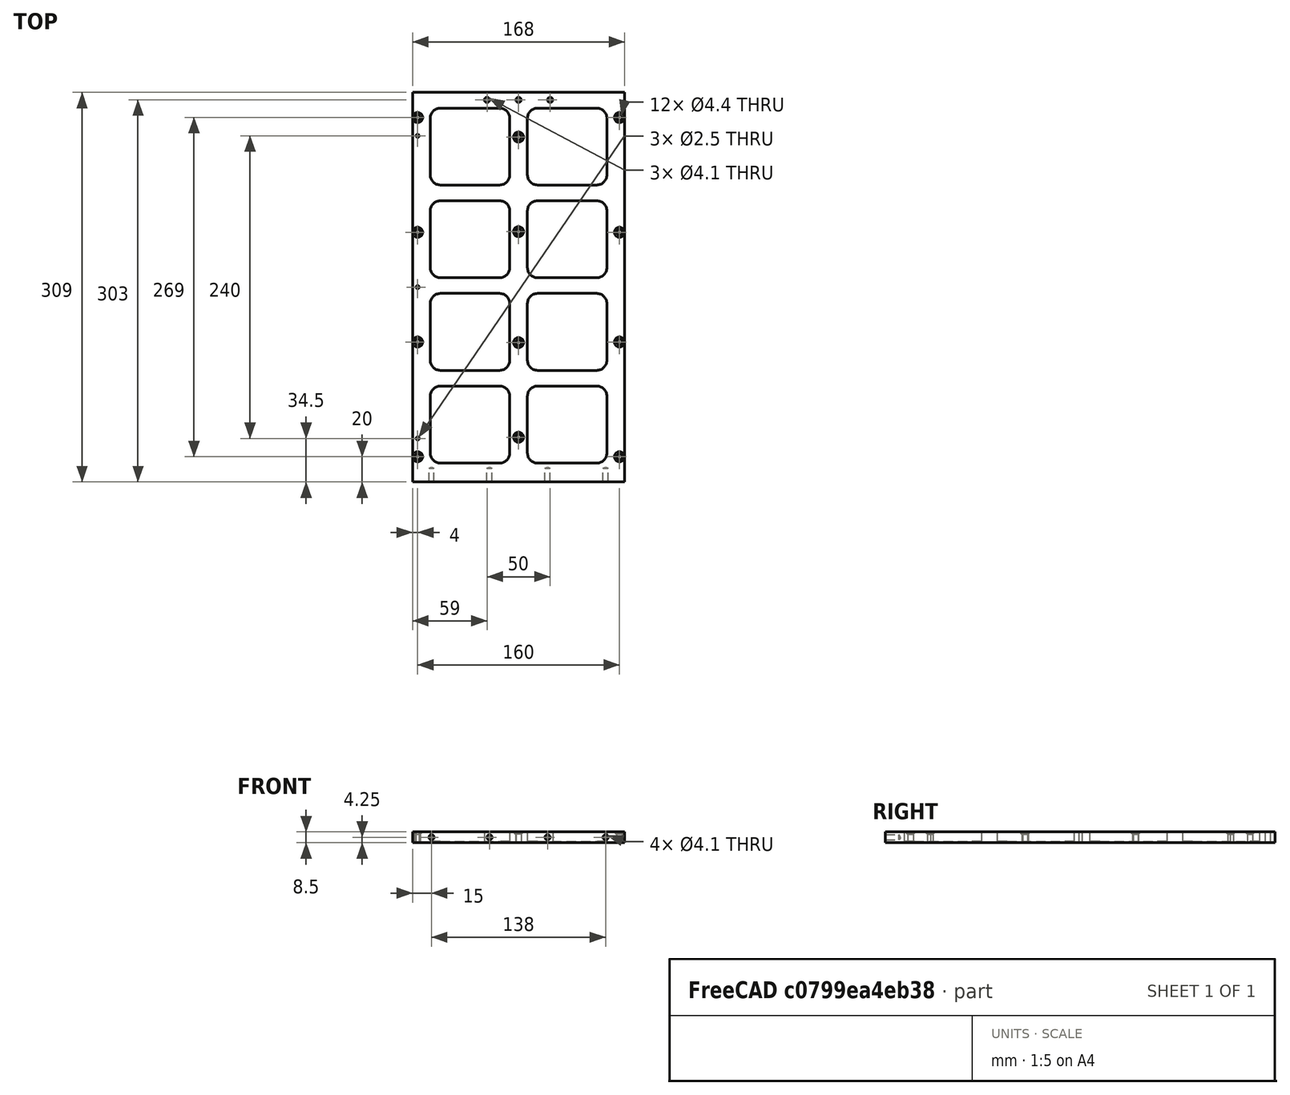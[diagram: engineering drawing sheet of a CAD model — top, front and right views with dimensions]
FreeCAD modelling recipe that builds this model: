
FCSTD DOCUMENT  (FreeCAD 0.18R14555 (Git shallow))
Label: y-plate
License: All rights reserved
LicenseURL: http://en.wikipedia.org/wiki/All_rights_reserved
objects: Sketcher::SketchObject×7, PartDesign::Hole×5, TechDraw::DrawViewDimension×4, TechDraw::DrawViewAnnotation×2, PartDesign::Pad×1, PartDesign::Pocket×1, PartDesign::Mirrored×1, PartDesign::Plane×1, PartDesign::Body×1, TechDraw::DrawSVGTemplate×1, TechDraw::DrawViewPart×1, TechDraw::DrawProjGroupItem×1, TechDraw::DrawProjGroup×1, TechDraw::DrawViewSection×1, TechDraw::DrawPage×1
note: 24 computed .brp shape members not serialized (recipe doc carries the construction recipe); baked Part::Feature solids carry a one-line shape summary decoded from their .brp

FEATURE [Sketcher::SketchObject] Sketch  label="plate"
  MapMode = 5
  Support = -> [XY_Plane]
  sketch-geometry (4):
    g0: LineSegment StartX=-84 StartY=154.5 StartZ=0 EndX=84 EndY=154.5 EndZ=0
    g1: LineSegment StartX=84 StartY=154.5 StartZ=0 EndX=84 EndY=-154.5 EndZ=0
    g2: LineSegment StartX=84 StartY=-154.5 StartZ=0 EndX=-84 EndY=-154.5 EndZ=0
    g3: LineSegment StartX=-84 StartY=-154.5 StartZ=0 EndX=-84 EndY=154.5 EndZ=0
  constraints (10):
    c: Coincident(g0,g1)
    c: Coincident(g1,g2)
    c: Coincident(g2,g3)
    c: Coincident(g3,g0)
    c: Horizontal(g2)
    c: Vertical(g3)
    c: DistanceY(g1,g1) = 309  'length'
    c: Symmetric(g0,g0,g-2)
    c: Symmetric(g1,g0,g-1)
    c: DistanceX(g0,g0) = 168  'width'
FEATURE [PartDesign::Pad] Pad
  Length = 8.5
  Length2 = 100
  Profile = -> Sketch
  Reversed = true
  Type = 0
FEATURE [Sketcher::SketchObject] Sketch001
  MapMode = 5
  Support = -> [XY_Plane]
  sketch-geometry (79):
    g0: LineSegment StartX=-62 StartY=-78.5 StartZ=0 EndX=-15 EndY=-78.5 EndZ=0
    g1: LineSegment StartX=-7 StartY=-86.5 StartZ=0 EndX=-7 EndY=-131.5 EndZ=0
    g2: LineSegment StartX=-15 StartY=-139.5 StartZ=0 EndX=-62 EndY=-139.5 EndZ=0
    g3: LineSegment StartX=-70 StartY=-131.5 StartZ=0 EndX=-70 EndY=-86.5 EndZ=0
    g4: ArcOfCircle CenterX=-15 CenterY=-86.5 CenterZ=0 NormalX=0 NormalY=0 NormalZ=1 AngleXU=0 Radius=8 StartAngle=1.7e-15 EndAngle=1.5708
    g5: ArcOfCircle CenterX=-15 CenterY=-131.5 CenterZ=0 NormalX=0 NormalY=0 NormalZ=1 AngleXU=0 Radius=8 StartAngle=4.71239 EndAngle=6.28319
    g6: ArcOfCircle CenterX=-62 CenterY=-131.5 CenterZ=0 NormalX=0 NormalY=0 NormalZ=1 AngleXU=0 Radius=8 StartAngle=3.14159 EndAngle=4.71239
    g7: ArcOfCircle CenterX=-62 CenterY=-86.5 CenterZ=0 NormalX=0 NormalY=0 NormalZ=1 AngleXU=0 Radius=8 StartAngle=1.5708 EndAngle=3.14159
    g8: LineSegment StartX=15 StartY=-78.5 StartZ=0 EndX=62 EndY=-78.5 EndZ=0
    g9: LineSegment StartX=70 StartY=-86.5 StartZ=0 EndX=70 EndY=-131.5 EndZ=0
    g10: LineSegment StartX=62 StartY=-139.5 StartZ=0 EndX=15 EndY=-139.5 EndZ=0
    g11: LineSegment StartX=7 StartY=-131.5 StartZ=0 EndX=7 EndY=-86.5 EndZ=0
    g12: ArcOfCircle CenterX=62 CenterY=-86.5 CenterZ=0 NormalX=0 NormalY=0 NormalZ=1 AngleXU=0 Radius=8 StartAngle=-1.8e-15 EndAngle=1.5708
    g13: ArcOfCircle CenterX=62 CenterY=-131.5 CenterZ=0 NormalX=0 NormalY=0 NormalZ=1 AngleXU=0 Radius=8 StartAngle=4.71239 EndAngle=6.28319
    g14: ArcOfCircle CenterX=15 CenterY=-131.5 CenterZ=0 NormalX=0 NormalY=0 NormalZ=1 AngleXU=0 Radius=8 StartAngle=3.14159 EndAngle=4.71239
    g15: ArcOfCircle CenterX=15 CenterY=-86.5 CenterZ=0 NormalX=0 NormalY=0 NormalZ=1 AngleXU=0 Radius=8 StartAngle=1.5708 EndAngle=3.14159
    g16: LineSegment [constr] StartX=7 StartY=-86.5 StartZ=0 EndX=-7 EndY=-86.5 EndZ=0
    g17: LineSegment [constr] StartX=84 StartY=-131.5 StartZ=0 EndX=-84 EndY=-131.5 EndZ=0
    g18: LineSegment [constr] StartX=84 StartY=-131.5 StartZ=0 EndX=70 EndY=-131.5 EndZ=0
    g19: LineSegment [constr] StartX=-84 StartY=-131.5 StartZ=0 EndX=-70 EndY=-131.5 EndZ=0
    g20: LineSegment StartX=-62 StartY=-5 StartZ=0 EndX=-15 EndY=-5 EndZ=0
    g21: LineSegment StartX=-7 StartY=-13 StartZ=0 EndX=-7 EndY=-58 EndZ=0
    g22: LineSegment StartX=-15 StartY=-66 StartZ=0 EndX=-62 EndY=-66 EndZ=0
    g23: LineSegment StartX=-70 StartY=-58 StartZ=0 EndX=-70 EndY=-13 EndZ=0
    g24: ArcOfCircle CenterX=-15 CenterY=-13 CenterZ=0 NormalX=0 NormalY=0 NormalZ=1 AngleXU=0 Radius=8 StartAngle=-1.8e-15 EndAngle=1.5708
    g25: ArcOfCircle CenterX=-15 CenterY=-58 CenterZ=0 NormalX=0 NormalY=0 NormalZ=1 AngleXU=0 Radius=8 StartAngle=4.71239 EndAngle=6.28319
    g26: ArcOfCircle CenterX=-62 CenterY=-58 CenterZ=0 NormalX=0 NormalY=0 NormalZ=1 AngleXU=0 Radius=8 StartAngle=3.14159 EndAngle=4.71239
    g27: ArcOfCircle CenterX=-62 CenterY=-13 CenterZ=0 NormalX=0 NormalY=0 NormalZ=1 AngleXU=0 Radius=8 StartAngle=1.5708 EndAngle=3.14159
    g28: LineSegment StartX=15 StartY=-5 StartZ=0 EndX=62 EndY=-5 EndZ=0
    g29: LineSegment StartX=70 StartY=-13 StartZ=0 EndX=70 EndY=-58 EndZ=0
    g30: LineSegment StartX=62 StartY=-66 StartZ=0 EndX=15 EndY=-66 EndZ=0
    g31: LineSegment StartX=7 StartY=-58 StartZ=0 EndX=7 EndY=-13 EndZ=0
    g32: ArcOfCircle CenterX=62 CenterY=-13 CenterZ=0 NormalX=0 NormalY=0 NormalZ=1 AngleXU=0 Radius=8 StartAngle=-9e-16 EndAngle=1.5708
    g33: ArcOfCircle CenterX=62 CenterY=-58 CenterZ=0 NormalX=0 NormalY=0 NormalZ=1 AngleXU=0 Radius=8 StartAngle=4.71239 EndAngle=6.28319
    g34: ArcOfCircle CenterX=15 CenterY=-58 CenterZ=0 NormalX=0 NormalY=0 NormalZ=1 AngleXU=0 Radius=8 StartAngle=3.14159 EndAngle=4.71239
    g35: ArcOfCircle CenterX=15 CenterY=-13 CenterZ=0 NormalX=0 NormalY=0 NormalZ=1 AngleXU=0 Radius=8 StartAngle=1.5708 EndAngle=3.14159
    g36: LineSegment [constr] StartX=-62 StartY=-154.5 StartZ=0 EndX=-62 EndY=154.5 EndZ=0
    g37: LineSegment StartX=-62 StartY=68.5 StartZ=0 EndX=-15 EndY=68.5 EndZ=0
    g38: LineSegment StartX=-7 StartY=60.5 StartZ=0 EndX=-7 EndY=15.5 EndZ=0
    g39: LineSegment StartX=-15 StartY=7.5 StartZ=0 EndX=-62 EndY=7.5 EndZ=0
    g40: LineSegment StartX=-70 StartY=15.5 StartZ=0 EndX=-70 EndY=60.5 EndZ=0
    g41: ArcOfCircle CenterX=-15 CenterY=60.5 CenterZ=0 NormalX=0 NormalY=0 NormalZ=1 AngleXU=0 Radius=8 StartAngle=-1.8e-15 EndAngle=1.5708
    g42: ArcOfCircle CenterX=-15 CenterY=15.5 CenterZ=0 NormalX=0 NormalY=0 NormalZ=1 AngleXU=0 Radius=8 StartAngle=4.71239 EndAngle=6.28319
    g43: ArcOfCircle CenterX=-62 CenterY=15.5 CenterZ=0 NormalX=0 NormalY=0 NormalZ=1 AngleXU=0 Radius=8 StartAngle=3.14159 EndAngle=4.71239
    g44: ArcOfCircle CenterX=-62 CenterY=60.5 CenterZ=0 NormalX=0 NormalY=0 NormalZ=1 AngleXU=0 Radius=8 StartAngle=1.5708 EndAngle=3.14159
    g45: LineSegment StartX=15 StartY=68.5 StartZ=0 EndX=62 EndY=68.5 EndZ=0
    g46: LineSegment StartX=70 StartY=60.5 StartZ=0 EndX=70 EndY=15.5 EndZ=0
    g47: LineSegment StartX=62 StartY=7.5 StartZ=0 EndX=15 EndY=7.5 EndZ=0
    g48: LineSegment StartX=7 StartY=15.5 StartZ=0 EndX=7 EndY=60.5 EndZ=0
    g49: ArcOfCircle CenterX=62 CenterY=60.5 CenterZ=0 NormalX=0 NormalY=0 NormalZ=1 AngleXU=0 Radius=8 StartAngle=-9e-16 EndAngle=1.5708
    g50: ArcOfCircle CenterX=62 CenterY=15.5 CenterZ=0 NormalX=0 NormalY=0 NormalZ=1 AngleXU=0 Radius=8 StartAngle=4.71239 EndAngle=6.28319
    g51: ArcOfCircle CenterX=15 CenterY=15.5 CenterZ=0 NormalX=0 NormalY=0 NormalZ=1 AngleXU=0 Radius=8 StartAngle=3.14159 EndAngle=4.71239
    g52: ArcOfCircle CenterX=15 CenterY=60.5 CenterZ=0 NormalX=0 NormalY=0 NormalZ=1 AngleXU=0 Radius=8 StartAngle=1.5708 EndAngle=3.14159
    g53: LineSegment [constr] StartX=-7 StartY=15.5 StartZ=0 EndX=7 EndY=15.5 EndZ=0
    g54: LineSegment [constr] StartX=-62 StartY=-154.5 StartZ=0 EndX=62 EndY=-154.5 EndZ=0
    g55: LineSegment [constr] StartX=62 StartY=-154.5 StartZ=0 EndX=62 EndY=-139.5 EndZ=0
    g56: LineSegment StartX=-62 StartY=142 StartZ=0 EndX=-15 EndY=142 EndZ=0
    g57: LineSegment StartX=-7 StartY=134 StartZ=0 EndX=-7 EndY=89 EndZ=0
    g58: LineSegment StartX=-15 StartY=81 StartZ=0 EndX=-62 EndY=81 EndZ=0
    g59: LineSegment StartX=-70 StartY=89 StartZ=0 EndX=-70 EndY=134 EndZ=0
    g60: ArcOfCircle CenterX=-15 CenterY=134 CenterZ=0 NormalX=0 NormalY=0 NormalZ=1 AngleXU=0 Radius=8 StartAngle=-1.8e-15 EndAngle=1.5708
    g61: ArcOfCircle CenterX=-15 CenterY=89 CenterZ=0 NormalX=0 NormalY=0 NormalZ=1 AngleXU=0 Radius=8 StartAngle=4.71239 EndAngle=6.28319
    g62: ArcOfCircle CenterX=-62 CenterY=89 CenterZ=0 NormalX=0 NormalY=0 NormalZ=1 AngleXU=0 Radius=8 StartAngle=3.14159 EndAngle=4.71239
    g63: ArcOfCircle CenterX=-62 CenterY=134 CenterZ=0 NormalX=0 NormalY=0 NormalZ=1 AngleXU=0 Radius=8 StartAngle=1.5708 EndAngle=3.14159
    g64: LineSegment StartX=15 StartY=142 StartZ=0 EndX=62 EndY=142 EndZ=0
    g65: LineSegment StartX=70 StartY=134 StartZ=0 EndX=70 EndY=89 EndZ=0
    g66: LineSegment StartX=62 StartY=81 StartZ=0 EndX=15 EndY=81 EndZ=0
    g67: LineSegment StartX=7 StartY=89 StartZ=0 EndX=7 EndY=134 EndZ=0
    g68: ArcOfCircle CenterX=62 CenterY=134 CenterZ=0 NormalX=0 NormalY=0 NormalZ=1 AngleXU=0 Radius=8 StartAngle=0 EndAngle=1.5708
    g69: ArcOfCircle CenterX=62 CenterY=89 CenterZ=0 NormalX=0 NormalY=0 NormalZ=1 AngleXU=0 Radius=8 StartAngle=4.71239 EndAngle=6.28319
    g70: ArcOfCircle CenterX=15 CenterY=89 CenterZ=0 NormalX=0 NormalY=0 NormalZ=1 AngleXU=0 Radius=8 StartAngle=3.14159 EndAngle=4.71239
    g71: ArcOfCircle CenterX=15 CenterY=134 CenterZ=0 NormalX=0 NormalY=0 NormalZ=1 AngleXU=0 Radius=8 StartAngle=1.5708 EndAngle=3.14159
    g72: LineSegment [constr] StartX=-7 StartY=89 StartZ=0 EndX=7 EndY=89 EndZ=0
    g73: LineSegment [constr] StartX=-62 StartY=154.5 StartZ=0 EndX=62 EndY=154.5 EndZ=0
    g74: LineSegment [constr] StartX=62 StartY=154.5 StartZ=0 EndX=62 EndY=142 EndZ=0
    g75: LineSegment [constr] StartX=62 StartY=81 StartZ=0 EndX=62 EndY=68.5 EndZ=0
    g76: LineSegment [constr] StartX=62 StartY=7.5 StartZ=0 EndX=62 EndY=-5 EndZ=0
    g77: LineSegment [constr] StartX=62 StartY=-66 StartZ=0 EndX=62 EndY=-78.5 EndZ=0
    g78: LineSegment [constr] StartX=-7 StartY=-58 StartZ=0 EndX=7 EndY=-58 EndZ=0
  constraints (197):
    c: Horizontal(g0)
    c: Horizontal(g2)
    c: Vertical(g1)
    c: Vertical(g3)
    c: Tangent(g0,g4) = 1.5708
    c: Tangent(g1,g4) = 1.5708
    c: Tangent(g1,g5) = 1.5708
    c: Tangent(g2,g5) = 1.5708
    c: Tangent(g2,g6) = 1.5708
    c: Tangent(g3,g6) = 1.5708
    c: Tangent(g3,g7) = 1.5708
    c: Tangent(g0,g7) = 1.5708
    c: Equal(g4,g5)
    c: Equal(g5,g6)
    c: Equal(g6,g7)
    c: DistanceX(g3,g1) = 63
    c: DistanceY(g2,g0) = 61  'length'
    c: Radius(g5) = 8
    c: Horizontal(g8)
    c: Horizontal(g10)
    c: Vertical(g9)
    c: Vertical(g11)
    c: Tangent(g8,g12) = 1.5708
    c: Tangent(g9,g12) = 1.5708
    c: Tangent(g9,g13) = 1.5708
    c: Tangent(g10,g13) = 1.5708
    c: Tangent(g10,g14) = 1.5708
    c: Tangent(g11,g14) = 1.5708
    c: Tangent(g11,g15) = 1.5708
    c: Tangent(g8,g15) = 1.5708
    c: Equal(g12,g13)
    c: Equal(g13,g14)
    c: Equal(g14,g15)
    c: DistanceX(g11,g9) = 63
    c: DistanceY(g10,g8) = 61
    c: Equal(g5,g13) = 8
    c: Coincident(g16,g11)
    c: Coincident(g16,g1)
    c: Horizontal(g16)
    c: Symmetric(g17,g17,g-2)
    c: DistanceX(g17,g17) = 168
    c: Coincident(g18,g17)
    c: Coincident(g19,g17)
    c: PointOnObject(g19,g3)
    c: Equal(g19,g16)
    c: Equal(g16,g18)
    c: Horizontal(g19)
    c: Horizontal(g18)
    c: Coincident(g18,g9)
    c: DistanceX(g1,g11) = 14
    c: DistanceX(g9,g17) = 14
    c: Horizontal(g20)
    c: Horizontal(g22)
    c: Vertical(g21)
    c: Vertical(g23)
    c: Tangent(g20,g24) = 1.5708
    c: Tangent(g21,g24) = 1.5708
    c: Tangent(g21,g25) = 1.5708
    c: Tangent(g22,g25) = 1.5708
    c: Tangent(g22,g26) = 1.5708
    c: Tangent(g23,g26) = 1.5708
    c: Tangent(g23,g27) = 1.5708
    c: Tangent(g20,g27) = 1.5708
    c: Equal(g24,g25)
    c: Equal(g25,g26)
    c: Equal(g26,g27)
    c: DistanceX(g23,g21) = 63
    c: DistanceY(g22,g20) = 61
    c: Equal(g5,g25) = 8
    c: Horizontal(g28)
    c: Horizontal(g30)
    c: Vertical(g29)
    c: Vertical(g31)
    c: Tangent(g28,g32) = 1.5708
    c: Tangent(g29,g32) = 1.5708
    c: Tangent(g29,g33) = 1.5708
    c: Tangent(g30,g33) = 1.5708
    c: Tangent(g30,g34) = 1.5708
    c: Tangent(g31,g34) = 1.5708
    c: Tangent(g31,g35) = 1.5708
    c: Tangent(g28,g35) = 1.5708
    c: Equal(g32,g33)
    c: Equal(g33,g34)
    c: Equal(g34,g35)
    c: DistanceX(g31,g29) = 63
    c: DistanceY(g30,g28) = 61
    c: Equal(g25,g33) = 8
    c: PointOnObject(g0,g36)
    c: PointOnObject(g22,g36)
    c: Symmetric(g36,g36,g-1)
    c: DistanceY(g36,g36) = 309
    c: Horizontal(g37)
    c: Horizontal(g39)
    c: Vertical(g38)
    c: Vertical(g40)
    c: Tangent(g37,g41) = 1.5708
    c: Tangent(g38,g41) = 1.5708
    c: Tangent(g38,g42) = 1.5708
    c: Tangent(g39,g42) = 1.5708
    c: Tangent(g39,g43) = 1.5708
    c: Tangent(g40,g43) = 1.5708
    c: Tangent(g40,g44) = 1.5708
    c: Tangent(g37,g44) = 1.5708
    c: Equal(g41,g42)
    c: Equal(g42,g43)
    c: Equal(g43,g44)
    c: DistanceX(g40,g38) = 63
    c: DistanceY(g39,g37) = 61
    c: Horizontal(g45)
    c: Horizontal(g47)
    c: Vertical(g46)
    c: Vertical(g48)
    c: Tangent(g45,g49) = 1.5708
    c: Tangent(g46,g49) = 1.5708
    c: Tangent(g46,g50) = 1.5708
    c: Tangent(g47,g50) = 1.5708
    c: Tangent(g47,g51) = 1.5708
    c: Tangent(g48,g51) = 1.5708
    c: Tangent(g48,g52) = 1.5708
    c: Tangent(g45,g52) = 1.5708
    c: Equal(g49,g50)
    c: Equal(g50,g51)
    c: Equal(g51,g52)
    c: DistanceX(g48,g46) = 63
    c: DistanceY(g47,g45) = 61
    c: Equal(g42,g50) = 8
    c: Coincident(g53,g38)
    c: Horizontal(g53)
    c: Coincident(g53,g48)
    c: PointOnObject(g39,g36)
    c: Coincident(g54,g36)
    c: Coincident(g55,g54)
    c: Coincident(g55,g10)
    c: Horizontal(g54)
    c: Vertical(g55)
    c: Horizontal(g56)
    c: Horizontal(g58)
    c: Vertical(g57)
    c: Vertical(g59)
    c: Tangent(g56,g60) = 1.5708
    c: Tangent(g57,g60) = 1.5708
    c: Tangent(g57,g61) = 1.5708
    c: Tangent(g58,g61) = 1.5708
    c: Tangent(g58,g62) = 1.5708
    c: Tangent(g59,g62) = 1.5708
    c: Tangent(g59,g63) = 1.5708
    c: Tangent(g56,g63) = 1.5708
    c: Equal(g60,g61)
    c: Equal(g61,g62)
    c: Equal(g62,g63)
    c: DistanceX(g59,g57) = 63
    c: DistanceY(g58,g56) = 61
    c: Horizontal(g64)
    c: Horizontal(g66)
    c: Vertical(g65)
    c: Vertical(g67)
    c: Tangent(g64,g68) = 1.5708
    c: Tangent(g65,g68) = 1.5708
    c: Tangent(g65,g69) = 1.5708
    c: Tangent(g66,g69) = 1.5708
    c: Tangent(g66,g70) = 1.5708
    c: Tangent(g67,g70) = 1.5708
    c: Tangent(g67,g71) = 1.5708
    c: Tangent(g64,g71) = 1.5708
    c: Equal(g68,g69)
    c: Equal(g69,g70)
    c: Equal(g70,g71)
    c: DistanceX(g67,g65) = 63
    c: DistanceY(g66,g64) = 61
    c: Equal(g61,g69) = 8
    c: Coincident(g72,g57)
    c: Horizontal(g72)
    c: Coincident(g72,g67)
    c: Coincident(g73,g36)
    c: Coincident(g74,g73)
    c: Coincident(g74,g64)
    c: Horizontal(g73)
    c: Vertical(g74)
    c: Coincident(g75,g66)
    c: Coincident(g75,g45)
    c: Vertical(g75)
    c: Coincident(g76,g47)
    c: Coincident(g76,g28)
    c: Vertical(g76)
    c: Coincident(g77,g30)
    c: Coincident(g77,g8)
    c: Vertical(g77)
    c: Equal(g77,g76)
    c: Equal(g76,g75)
    c: Equal(g75,g74)
    c: Equal(g62,g44)
    c: Equal(g44,g27)
    c: PointOnObject(g58,g36)
    c: Coincident(g78,g21)
    c: Coincident(g78,g31)
    c: Horizontal(g78)
    c: DistanceY(g55,g55) = 15
FEATURE [PartDesign::Pocket] Pocket
  BaseFeature = -> Pad
  Length = 7.5
  Length2 = 100
  Profile = -> Sketch001
  Type = 0
FEATURE [Sketcher::SketchObject] Sketch002
  MapMode = 5
  Support = -> [XY_Plane]
  expr: Constraints[6] = <<plate>>.Constraints.length
  expr: Constraints[11] = <<plate>>.Constraints.width / 2
  sketch-geometry (9):
    g0: Circle CenterX=80 CenterY=134.5 CenterZ=0 NormalX=0 NormalY=0 NormalZ=1 AngleXU=0 Radius=2
    g1: Circle CenterX=80 CenterY=43.5 CenterZ=0 NormalX=0 NormalY=0 NormalZ=1 AngleXU=0 Radius=2
    g2: Circle CenterX=80 CenterY=-43.5 CenterZ=0 NormalX=0 NormalY=0 NormalZ=1 AngleXU=0 Radius=2
    g3: Circle CenterX=80 CenterY=-134.5 CenterZ=0 NormalX=0 NormalY=0 NormalZ=1 AngleXU=0 Radius=2
    g4: LineSegment [constr] StartX=80 StartY=154.5 StartZ=0 EndX=80 EndY=134.5 EndZ=0
    g5: LineSegment [constr] StartX=80 StartY=-134.5 StartZ=0 EndX=80 EndY=-154.5 EndZ=0
    g6: LineSegment [constr] StartX=84 StartY=154.5 StartZ=0 EndX=80 EndY=154.5 EndZ=0
    g7: LineSegment [constr] StartX=80 StartY=134.5 StartZ=0 EndX=80 EndY=43.5 EndZ=0
    g8: LineSegment [constr] StartX=80 StartY=-43.5 StartZ=0 EndX=80 EndY=-134.5 EndZ=0
  constraints (24):
    c: Vertical(g4)
    c: Coincident(g0,g4)
    c: Equal(g0,g1)
    c: Equal(g1,g2)
    c: Equal(g2,g3)
    c: Diameter(g0) = 4
    c: DistanceY(g5,g4) = 309
    c: Symmetric(g4,g5,g-1)
    c: Equal(g5,g4)
    c: Horizontal(g6)
    c: Coincident(g6,g4)
    c: DistanceX(g-1,g6) = 84
    c: DistanceX(g6,g6) = 4
    c: DistanceY(g5,g3) = 20
    c: Coincident(g3,g5)
    c: Vertical(g5)
    c: Coincident(g7,g0)
    c: Coincident(g7,g1)
    c: Vertical(g7)
    c: Coincident(g8,g2)
    c: Coincident(g8,g3)
    c: Vertical(g8)
    c: Equal(g8,g7)
    c: DistanceY(g1,g4) = 111
FEATURE [PartDesign::Hole] Hole
  BaseFeature = -> Pocket
  Depth = 25
  DepthType = 0
  Diameter = 4.4
  DrillPoint = 1
  DrillPointAngle = 118
  HoleCutCountersinkAngle = 90
  HoleCutDepth = 0
  HoleCutDiameter = 8
  HoleCutType = 2
  ModelActualThread = false
  Profile = -> Sketch002
  Tapered = false
  TaperedAngle = 90
  ThreadAngle = 0
  ThreadClass = 0
  ThreadCutOffInner = 0
  ThreadCutOffOuter = 0
  ThreadDirection = 0
  ThreadFit = 0
  ThreadPitch = 0
  ThreadSize = 5
  ThreadType = 1
  Threaded = false
FEATURE [PartDesign::Mirrored] Mirrored
  BaseFeature = -> Hole
  MirrorPlane = -> Sketch002 [V_Axis]
  Originals = -> [Hole]
FEATURE [PartDesign::Plane] DatumPlane
  AttachmentOffset = pos=(0,0,154.5) rot=(0,0,1;0rad)
  Length = 179.593
  MapMode = 5
  Placement = pos=(0,-154.5,-3.43e-14) rot=(1,0,0;1.5708rad)
  ResizeMode = 0
  Support = -> [XZ_Plane]
  Width = 31.5931
FEATURE [Sketcher::SketchObject] Sketch003
  MapMode = 5
  Placement = pos=(0,-154.5,-3.43e-14) rot=(1,0,0;1.5708rad)
  Support = -> [DatumPlane]
  expr: Constraints[14] = <<plate>>.Constraints.width
  sketch-geometry (9):
    g0: Circle CenterX=-69 CenterY=-4.25 CenterZ=0 NormalX=0 NormalY=0 NormalZ=1 AngleXU=0 Radius=2
    g1: Circle CenterX=-23 CenterY=-4.25 CenterZ=0 NormalX=0 NormalY=0 NormalZ=1 AngleXU=0 Radius=2
    g2: Circle CenterX=23 CenterY=-4.25 CenterZ=0 NormalX=0 NormalY=0 NormalZ=1 AngleXU=0 Radius=2
    g3: Circle CenterX=69 CenterY=-4.25 CenterZ=0 NormalX=0 NormalY=0 NormalZ=1 AngleXU=0 Radius=2
    g4: LineSegment [constr] StartX=-69 StartY=-4.25 StartZ=0 EndX=-23 EndY=-4.25 EndZ=0
    g5: LineSegment [constr] StartX=-23 StartY=-4.25 StartZ=0 EndX=23 EndY=-4.25 EndZ=0
    g6: LineSegment [constr] StartX=69 StartY=-4.25 StartZ=0 EndX=23 EndY=-4.25 EndZ=0
    g7: LineSegment [constr] StartX=69 StartY=-4.25 StartZ=0 EndX=84 EndY=-4.25 EndZ=0
    g8: LineSegment [constr] StartX=-69 StartY=-4.25 StartZ=0 EndX=-84 EndY=-4.25 EndZ=0
  constraints (25):
    c: Coincident(g4,g0)
    c: Coincident(g4,g1)
    c: Horizontal(g4)
    c: Coincident(g5,g1)
    c: Coincident(g5,g2)
    c: Coincident(g6,g3)
    c: Coincident(g6,g2)
    c: Coincident(g7,g3)
    c: Horizontal(g7)
    c: Coincident(g8,g0)
    c: Horizontal(g8)
    c: Horizontal(g5)
    c: Equal(g4,g5)
    c: Equal(g5,g6)
    c: DistanceX(g8,g7) = 168
    c: DistanceY(g8,g-1) = 4.25
    c: Equal(g0,g1)
    c: Equal(g1,g2)
    c: Equal(g2,g3)
    c: Diameter(g3) = 4
    c: Symmetric(g7,g8,g-2)
    c: DistanceX(g0,g-1) = 69
    c: DistanceX(g1,g-1) = 23
    c: DistanceX(g8,g0) = 15
    c: Equal(g7,g8)
FEATURE [Sketcher::SketchObject] Sketch004
  MapMode = 5
  Support = -> [XY_Plane]
  expr: Constraints[18] = <<plate>>.Constraints.length
  sketch-geometry (9):
    g0: Circle CenterX=0 CenterY=119 CenterZ=0 NormalX=0 NormalY=0 NormalZ=1 AngleXU=0 Radius=2
    g1: Circle CenterX=0 CenterY=44 CenterZ=0 NormalX=0 NormalY=0 NormalZ=1 AngleXU=0 Radius=2
    g2: Circle CenterX=0 CenterY=-44 CenterZ=0 NormalX=0 NormalY=0 NormalZ=1 AngleXU=0 Radius=2
    g3: Circle CenterX=0 CenterY=-119 CenterZ=0 NormalX=0 NormalY=0 NormalZ=1 AngleXU=0 Radius=2
    g4: LineSegment [constr] StartX=0 StartY=154.5 StartZ=0 EndX=0 EndY=119 EndZ=0
    g5: LineSegment [constr] StartX=0 StartY=119 StartZ=0 EndX=0 EndY=44 EndZ=0
    g6: LineSegment [constr] StartX=0 StartY=44 StartZ=0 EndX=0 EndY=-44 EndZ=0
    g7: LineSegment [constr] StartX=0 StartY=-44 StartZ=0 EndX=0 EndY=-119 EndZ=0
    g8: LineSegment [constr] StartX=0 StartY=-119 StartZ=0 EndX=0 EndY=-154.5 EndZ=0
  constraints (23):
    c: Diameter(g0) = 4
    c: Equal(g0,g1)
    c: Equal(g0,g2)
    c: Equal(g0,g3)
    c: PointOnObject(g4,g-2)
    c: Coincident(g4,g0)
    c: Vertical(g4)
    c: Coincident(g5,g0)
    c: Coincident(g5,g1)
    c: Vertical(g5)
    c: Coincident(g5,g6)
    c: Coincident(g6,g2)
    c: Vertical(g6)
    c: Coincident(g6,g7)
    c: Coincident(g7,g3)
    c: Vertical(g7)
    c: Coincident(g7,g8)
    c: Symmetric(g8,g4,g-1)
    c: DistanceY(g8,g4) = 309
    c: DistanceY(g4,g4) = 35.5
    c: DistanceY(g1,g4) = 110.5
    c: Equal(g4,g8)
    c: Equal(g7,g5)
FEATURE [PartDesign::Hole] Hole001
  BaseFeature = -> Mirrored
  Depth = 25
  DepthType = 0
  Diameter = 4.4
  DrillPoint = 1
  DrillPointAngle = 118
  HoleCutCountersinkAngle = 90
  HoleCutDepth = 0
  HoleCutDiameter = 8
  HoleCutType = 2
  ModelActualThread = false
  Profile = -> Sketch004
  Tapered = false
  TaperedAngle = 90
  ThreadAngle = 0
  ThreadClass = 0
  ThreadCutOffInner = 0
  ThreadCutOffOuter = 0
  ThreadDirection = 0
  ThreadFit = 0
  ThreadPitch = 0
  ThreadSize = 5
  ThreadType = 1
  Threaded = false
FEATURE [PartDesign::Hole] Hole002
  BaseFeature = -> Hole001
  Depth = 12
  DepthType = 0
  Diameter = 4.1
  DrillPoint = 1
  DrillPointAngle = 118
  HoleCutCountersinkAngle = 90
  HoleCutDepth = 0
  HoleCutDiameter = 0
  HoleCutType = 0
  ModelActualThread = false
  Profile = -> Sketch003
  Tapered = false
  TaperedAngle = 90
  ThreadAngle = 0
  ThreadClass = 0
  ThreadCutOffInner = 0
  ThreadCutOffOuter = 0
  ThreadDirection = 0
  ThreadFit = 0
  ThreadPitch = 0
  ThreadSize = 0
  ThreadType = 0
  Threaded = false
FEATURE [Sketcher::SketchObject] Sketch005
  MapMode = 5
  Support = -> [XY_Plane]
  expr: Constraints[11] = <<plate>>.Constraints.length / 2
  sketch-geometry (6):
    g0: Circle CenterX=25 CenterY=148.5 CenterZ=0 NormalX=0 NormalY=0 NormalZ=1 AngleXU=0 Radius=2
    g1: Circle CenterX=0 CenterY=148.5 CenterZ=0 NormalX=0 NormalY=0 NormalZ=1 AngleXU=0 Radius=2
    g2: Circle CenterX=-25 CenterY=148.5 CenterZ=0 NormalX=0 NormalY=0 NormalZ=1 AngleXU=0 Radius=2
    g3: LineSegment [constr] StartX=-25 StartY=148.5 StartZ=0 EndX=0 EndY=148.5 EndZ=0
    g4: LineSegment [constr] StartX=0 StartY=148.5 StartZ=0 EndX=25 EndY=148.5 EndZ=0
    g5: LineSegment [constr] StartX=0 StartY=154.5 StartZ=0 EndX=0 EndY=148.5 EndZ=0
  constraints (16):
    c: PointOnObject(g1,g-2)
    c: Coincident(g3,g2)
    c: Coincident(g3,g1)
    c: Coincident(g4,g1)
    c: Coincident(g4,g0)
    c: Horizontal(g4)
    c: Horizontal(g3)
    c: Equal(g1,g0)
    c: Equal(g0,g2)
    c: DistanceX(g2,g0) = 50
    c: Vertical(g5)
    c: DistanceY(g-1,g5) = 154.5
    c: Coincident(g5,g1)
    c: DistanceY(g5,g5) = 6
    c: Diameter(g0) = 4
    c: Equal(g4,g3)
FEATURE [PartDesign::Hole] Hole003
  BaseFeature = -> Hole002
  Depth = 25
  DepthType = 1
  Diameter = 4.1
  DrillPoint = 1
  DrillPointAngle = 118
  HoleCutCountersinkAngle = 90
  HoleCutDepth = 0
  HoleCutDiameter = 0
  HoleCutType = 0
  ModelActualThread = false
  Profile = -> Sketch005
  Tapered = false
  TaperedAngle = 90
  ThreadAngle = 0
  ThreadClass = 0
  ThreadCutOffInner = 0
  ThreadCutOffOuter = 0
  ThreadDirection = 0
  ThreadFit = 0
  ThreadPitch = 0
  ThreadSize = 0
  ThreadType = 0
  Threaded = false
FEATURE [Sketcher::SketchObject] Sketch006
  MapMode = 5
  Support = -> [XY_Plane]
  expr: Constraints[10] = <<plate>>.Constraints.width / 2
  sketch-geometry (5):
    g0: Circle CenterX=-80 CenterY=120 CenterZ=0 NormalX=0 NormalY=0 NormalZ=1 AngleXU=0 Radius=1.5
    g1: Circle CenterX=-80 CenterY=0 CenterZ=0 NormalX=0 NormalY=0 NormalZ=1 AngleXU=0 Radius=1.5
    g2: Circle CenterX=-80 CenterY=-120 CenterZ=0 NormalX=0 NormalY=0 NormalZ=1 AngleXU=0 Radius=1.5
    g3: LineSegment [constr] StartX=-80 StartY=120 StartZ=0 EndX=-80 EndY=-120 EndZ=0
    g4: LineSegment [constr] StartX=-80 StartY=0 StartZ=0 EndX=-84 EndY=0 EndZ=0
  constraints (13):
    c: Diameter(g0) = 3
    c: Equal(g0,g1)
    c: Equal(g0,g2)
    c: Coincident(g3,g0)
    c: Coincident(g3,g2)
    c: PointOnObject(g1,g3)
    c: PointOnObject(g1,g-1)
    c: Symmetric(g0,g2,g-1)
    c: Coincident(g4,g1)
    c: Horizontal(g4)
    c: DistanceX(g4,g-1) = 84
    c: DistanceX(g4,g4) = 4
    c: DistanceY(g-1,g0) = 120
FEATURE [PartDesign::Hole] Hole004
  BaseFeature = -> Hole003
  Depth = 25
  DepthType = 0
  Diameter = 2.5
  DrillPoint = 1
  DrillPointAngle = 118
  HoleCutCountersinkAngle = 90
  HoleCutDepth = 0
  HoleCutDiameter = 3
  HoleCutType = 0
  ModelActualThread = false
  Profile = -> Sketch006
  Tapered = false
  TaperedAngle = 90
  ThreadAngle = 60
  ThreadClass = 0
  ThreadCutOffInner = 0.0541266
  ThreadCutOffOuter = 0.108253
  ThreadDirection = 1
  ThreadFit = 0
  ThreadPitch = 0.5
  ThreadSize = 3
  ThreadType = 1
  Threaded = true
FEATURE [PartDesign::Body] Body
  Group = -> [Sketch,Pad,Sketch001,Pocket,Sketch002,Hole,Mirrored,DatumPlane,Sketch003,Sketch004,Hole001,Hole002,Sketch005,Hole003,Sketch006,Hole004]
  Origin = -> Origin
  Tip = -> Hole004
FEATURE [TechDraw::DrawSVGTemplate] Template
  EditableTexts = Designed_by_Name=A. Ampatzoglou; FC-Date=26/11/2019; FC-SC=1:2; FC-SHEET=1/1; FC-Title=Deployer - Y Plate; MATERIAL=NOTE-1; REV=B; ROUGHNESS=-; Subtitle=y-plate; TOLERANCES=DIN ISO 2768 - mk; Weight=~0.67kg
  Height = 210
  Orientation = 1
  Width = 297
FEATURE [TechDraw::DrawViewPart] View
  CoarseView = false
  Direction = (0.634,-0.502,0.588)
  Focus = 100
  HardHidden = false
  IsoCount = 0
  IsoHidden = false
  IsoVisible = false
  LockPosition = false
  Perspective = false
  Rotation = 0
  Scale = 0.2
  ScaleType = 0
  SeamHidden = false
  SeamVisible = false
  SmoothHidden = false
  SmoothVisible = false
  Source = -> [Body]
  X = 250.932
  Y = 173.975
FEATURE [TechDraw::DrawViewAnnotation] Annotation  label="SCALE"
  Font = DejaVu Sans
  LineSpace = 80
  LockPosition = false
  MaxWidth = -1
  Rotation = 0
  ScaleType = 0
  Text = SCALE 0.2
  TextSize = 6
  TextStyle = 0
  X = 269.43
  Y = 139.92
FEATURE [TechDraw::DrawProjGroupItem] ProjItem  label="Front"
  CoarseView = false
  Direction = (0,-1,0)
  Focus = 100
  HardHidden = false
  IsoCount = 0
  IsoHidden = false
  IsoVisible = false
  LockPosition = true
  Perspective = false
  Rotation = 0
  RotationVector = (1,0,0)
  Scale = 0.5
  ScaleType = 2
  SeamHidden = false
  SeamVisible = false
  SmoothHidden = false
  SmoothVisible = false
  Source = -> [Body]
  Type = 0
  X = 0
  Y = 0
FEATURE [TechDraw::DrawProjGroup] ProjGroup
  Anchor = -> ProjItem
  AutoDistribute = true
  LockPosition = false
  ProjectionType = 1
  Rotation = 0
  Scale = 0.5
  ScaleType = 2
  Source = -> [Body]
  Views = -> [ProjItem]
  X = 166.844
  Y = 177.461
  spacingX = 15
  spacingY = 15
FEATURE [TechDraw::DrawViewSection] DrawViewSection  label="Section A - A"
  BaseView = -> ProjItem
  CoarseView = false
  Direction = (0,0,-1)
  FileHatchPattern = <path>
  Focus = 100
  FuseBeforeCut = true
  HardHidden = false
  HatchScale = 1
  IsoCount = 0
  IsoHidden = false
  IsoVisible = false
  LockPosition = false
  NameGeomPattern = Diamond
  Perspective = false
  Rotation = 0
  Scale = 0.5
  ScaleType = 0
  SeamHidden = false
  SeamVisible = false
  SectionDirection = 2
  SectionNormal = (0,0,-1)
  SectionOrigin = (0,0,-4.25)
  SectionSymbol = A
  SmoothHidden = false
  SmoothVisible = false
  Source = -> [Body]
  X = 73.2214
  Y = 109.584
FEATURE [TechDraw::DrawViewAnnotation] Annotation001
  Font = DejaVu Sans
  LineSpace = 80
  LockPosition = false
  MaxWidth = -1
  Rotation = 0
  ScaleType = 0
  Text = Notes: | 1. Material: Al 7075 | 2. Drill Hole \u23004.4 THRU for M4 DIN  | 7991 | 3. Drill Hole \u23004.1 for M4x0.7x2D  | HELICOIL insert | 4. Drill Hole \u23004.1 for M4x0.7x1.5D | HELICOIL insert. HELICOIL insert must |  be aligned with reference plane A | 5. Tapping Drill \u23002.5 THRU for  | M3x0.5 | 6. This part is mating with flange,  | x-plate and rail
  TextSize = 6
  TextStyle = 0
  X = 199.319
  Y = 106.299
FEATURE [TechDraw::DrawViewDimension] Dimension
  Arbitrary = false
  FormatSpec = ⌀%.2f (Note-3)
  LockPosition = false
  MeasureType = 1
  OverTolerance = 0
  References2D = -> [ProjItem]
  Rotation = 0
  ScaleType = 0
  Type = 5
  UnderTolerance = 0
  X = 1.68749
  Y = 13.2283
FEATURE [TechDraw::DrawViewDimension] Dimension001
  Arbitrary = false
  FormatSpec = ⌀%.2f (Note-2)
  LockPosition = false
  MeasureType = 1
  OverTolerance = 0
  References2D = -> [DrawViewSection]
  Rotation = 0
  ScaleType = 0
  Type = 5
  UnderTolerance = 0
  X = 63.7857
  Y = -45.7061
FEATURE [TechDraw::DrawViewDimension] Dimension002
  Arbitrary = false
  FormatSpec = ⌀%.2f (Note-4)
  LockPosition = false
  MeasureType = 1
  OverTolerance = 0
  References2D = -> [DrawViewSection]
  Rotation = 0
  ScaleType = 0
  Type = 5
  UnderTolerance = 0
  X = 51.4157
  Y = -85.3987
FEATURE [TechDraw::DrawViewDimension] Dimension003
  Arbitrary = false
  FormatSpec = ⌀%.2f (NOTE-5)
  LockPosition = false
  MeasureType = 1
  OverTolerance = 0
  References2D = -> [DrawViewSection]
  Rotation = 0
  ScaleType = 0
  Type = 5
  UnderTolerance = 0
  X = -6.80394
  Y = -90.2902
FEATURE [TechDraw::DrawPage] Page
  KeepUpdated = true
  ProjectionType = 0
  Template = -> Template
  Views = -> [View,Annotation,ProjGroup,DrawViewSection,Annotation001,Dimension,Dimension001,Dimension002,Dimension003]
note: 1 file-system path scrubbed to <path> (originals preserved in the JSON sidecar)
